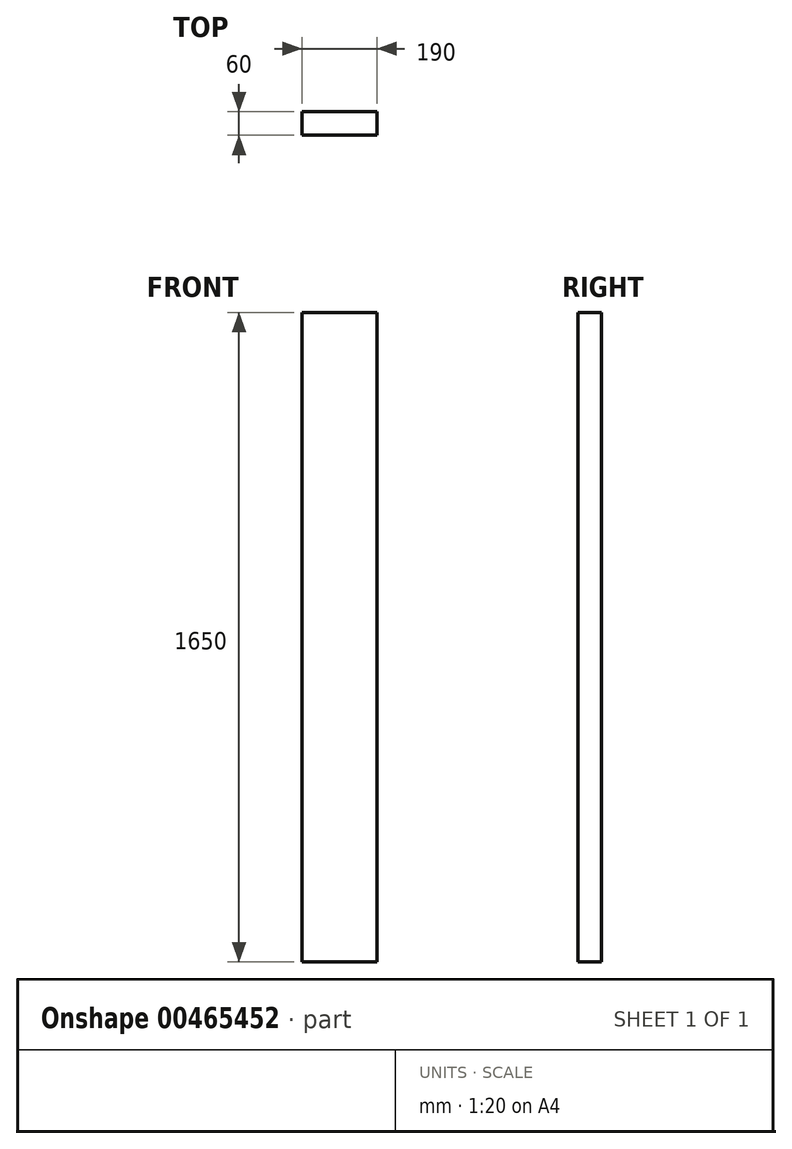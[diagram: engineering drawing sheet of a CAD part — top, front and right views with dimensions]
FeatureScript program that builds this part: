
annotation { "Feature Type Name" : "Feature", "Feature Type Description" : "" }
export const myFeature = defineFeature(function(context is Context, id is Id, definition is map)
    precondition{}
    {
        {
            var Q0;
            Q0=qCreatedBy(makeId("Front.planeOp"),FACE);
            var sketch = newSketch(context, id + "F0", { "sketchPlane" : qUnion([Q0])});
            skLineSegment(sketch, "E0.bottom", {"start": v(190, -3574.72) * mm, "end": v(0, -3574.72) * mm});
            skLineSegment(sketch, "E0.top", {"start": v(190, -5224.72) * mm, "end": v(0, -5224.72) * mm});
            skLineSegment(sketch, "E0.left", {"start": v(190, -3574.72) * mm, "end": v(190, -5224.72) * mm});
            skLineSegment(sketch, "E0.right", {"start": v(0, -3574.72) * mm, "end": v(0, -5224.72) * mm});
            skSolve(sketch);
        }
        {
            var Q0;
            Q0=makeQuery(id+"F0.imprint","IMPRINT",FACE,{"disambiguationData":[TD([[makeQuery(id+"F0.imprint","IMPRINT",EDGE,{"derivedFrom":sQuery(id+"F0.wireOp",EDGE,"E0.bottom")}),1.0]])]});
            extrude(context, id + "F1", {"entities" : qUnion([Q0]), "depth" : 60 * mm});
        }
    });
